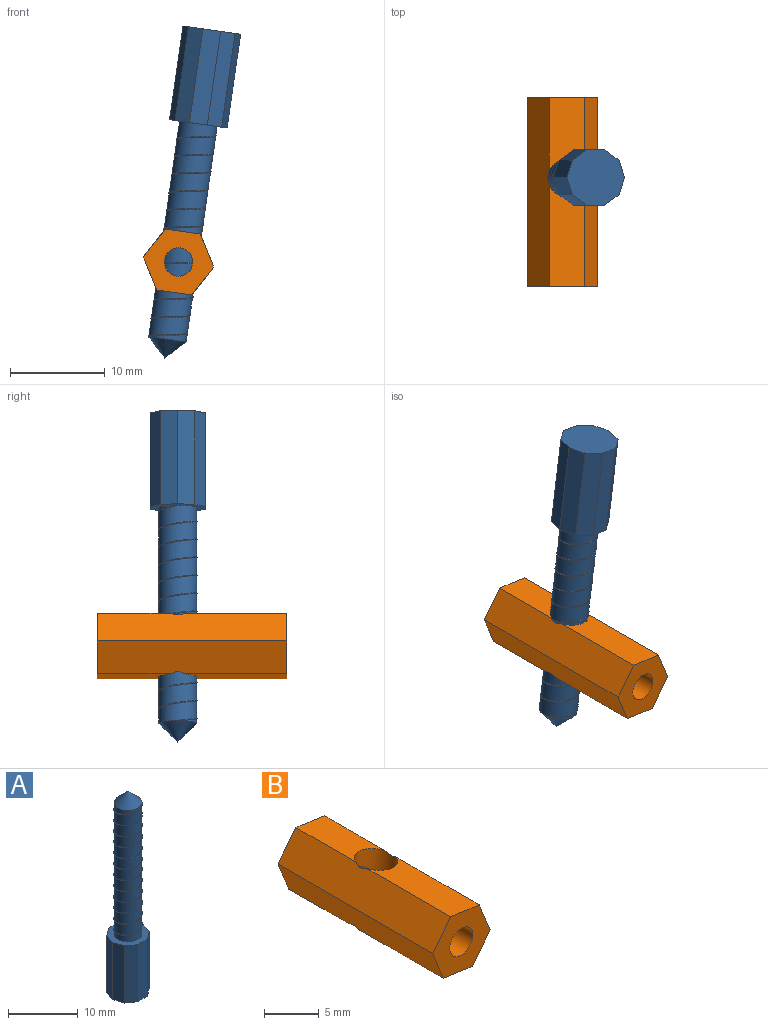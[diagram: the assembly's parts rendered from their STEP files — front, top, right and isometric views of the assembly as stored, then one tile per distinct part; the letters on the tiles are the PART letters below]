
ASSEMBLY  parts=2 mates=1
PART A: 19 faces, bbox 6.2x5.9x35 mm
  f0: cylinder r=2mm len=23mm, axis (0,0,-1), area 286.4mm2, adj f11,f13,f15,f16,f17,f18
  f1: plane 10x1.54mm, normal (0.59,-0.81,0), area 19mm2, adj f2,f10,f11,f12
  f2: plane 10x1.81mm, normal (0.95,-0.31,0), area 19mm2, adj f1,f3,f11,f12
  f3: plane 10x1.81mm, normal (0.95,0.31,0), area 19mm2, adj f2,f4,f11,f12
  f4: plane 10x1.54mm, normal (0.59,0.81,0), area 19mm2, adj f3,f5,f11,f12
  f5: plane 10x1.9mm, normal (0,1,0), area 19mm2, adj f4,f6,f11,f12
  f6: plane 10x1.54mm, normal (-0.59,0.81,0), area 19mm2, adj f5,f7,f11,f12
  f7: plane 10x1.81mm, normal (-0.95,0.31,0), area 19mm2, adj f6,f8,f11,f12
  f8: plane 10x1.81mm, normal (-0.95,-0.31,0), area 19mm2, adj f7,f9,f11,f12
  f9: plane 10x1.54mm, normal (-0.59,-0.81,0), area 19mm2, adj f8,f10,f11,f12
  f10: plane 10x1.9mm, normal (0,-1,0), area 19mm2, adj f1,f9,f11,f12
  f11: plane 6.15x5.85mm, normal (0,0,1), area 15.2mm2, adj f0,f1,f2,f3,f4,f5,f6,f7
  f12: plane 6.15x5.85mm, normal (0,0,-1), area 27.8mm2, adj f1,f2,f3,f4,f5,f6,f7,f8
  f13: cone r=2mm half-angle=45deg, axis (0,0,-1), area 17.8mm2, adj f0,f14
  f14: cylinder r=2mm len=0.31mm, axis (0,0,1), area 0mm2, adj f13,f16,f17
  f15: plane 0.05x0.05mm, normal (0,-1,0), area 0mm2, adj f0,f11,f17,f18
  f16: plane 0.09x0.05mm, normal (0,1,0), area 0mm2, adj f0,f14,f17,f18
  f17: bspline ~23.04x4.73mm, area 9.8mm2, adj f0,f14,f15,f16,f18
  f18: bspline ~23.05x4.73mm, area 10.4mm2, adj f0,f11,f15,f16,f17
PART B: 13 faces, bbox 7.4x20x7 mm
  f0: plane 10.81x3.71mm, normal (-0.14,0,-0.99), area 37mm2, adj f5,f9,f10,f12
  f1: plane 7.81x3.71mm, normal (0.14,0,0.99), area 25.7mm2, adj f6,f8,f11,f12
  f2: cylinder r=1.5mm len=10.18mm, axis (0,1,0), area 92.6mm2, adj f10,f12
  f3: cylinder r=1.5mm len=7.18mm, axis (0,1,0), area 64.3mm2, adj f11,f12
  f4: plane 7.81x3.71mm, normal (-0.14,0,-0.99), area 25.7mm2, adj f5,f9,f11,f12
  f5: plane 20x2.95mm, normal (0.79,0,-0.62), area 74.8mm2, adj f0,f4,f6,f10,f11,f12
  f6: plane 20x3.48mm, normal (0.93,0,0.37), area 74.8mm2, adj f1,f5,f7,f10,f11,f12
  f7: plane 10.81x3.71mm, normal (0.14,0,0.99), area 37mm2, adj f6,f8,f10,f12
  f8: plane 20x2.95mm, normal (-0.79,0,0.62), area 74.8mm2, adj f1,f7,f9,f10,f11,f12
  f9: plane 20x3.48mm, normal (-0.93,0,-0.37), area 74.8mm2, adj f0,f4,f8,f10,f11,f12
  f10: plane 7.43x6.97mm, normal (0,-1,0), area 29.5mm2, adj f0,f2,f5,f6,f7,f8,f9
  f11: plane 7.43x6.97mm, normal (0,1,0), area 29.5mm2, adj f1,f3,f4,f5,f6,f8,f9
  f12: cylinder r=2mm len=7mm, axis (0.14,0,0.99), area 65.4mm2, adj f0,f1,f2,f3,f4,f5,f6,f7
PLACE A rot(axis=(0,-1,0),171.8deg) t=(1.39,-8.42,9.78)mm
PLACE B t=(-2.12,0.08,-14.72)mm
MATE cylindrical A.f0 <-> B.f12  axis (0.14,0,0.99) through (-1.66,-8.42,-11.5)mm
